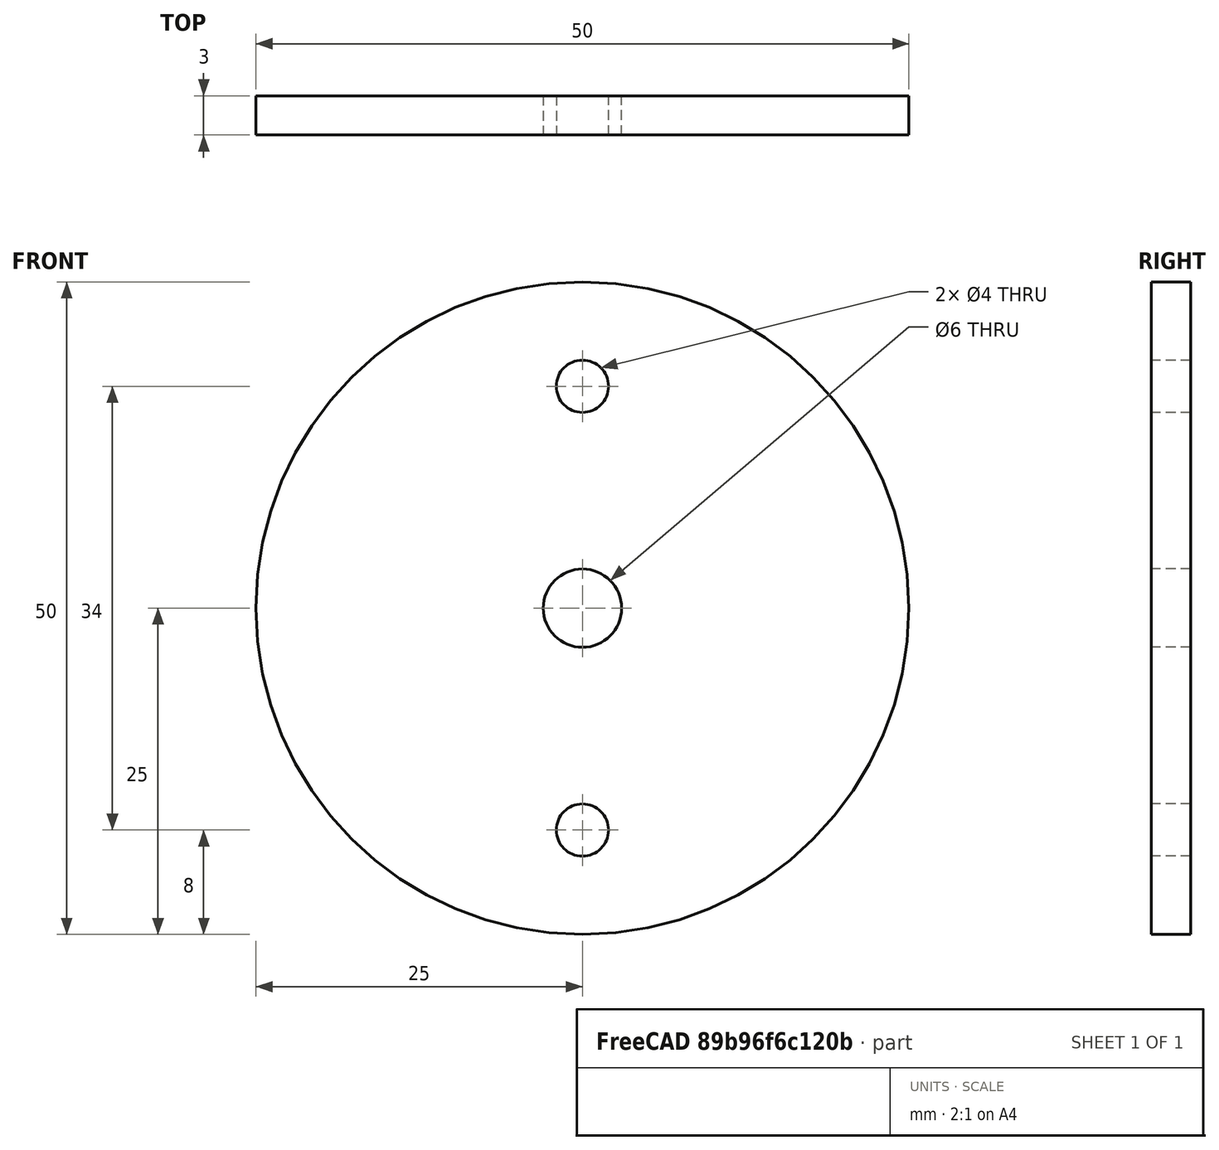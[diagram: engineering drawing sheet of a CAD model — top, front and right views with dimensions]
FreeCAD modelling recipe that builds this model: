
FCSTD DOCUMENT  (FreeCAD 0.15R4669 (Git))
Label: BR_plaqueRoue
License: All rights reserved
LicenseURL: http://en.wikipedia.org/wiki/All_rights_reserved
objects: Sketcher::SketchObject×1, Part::Extrusion×1
note: 2 computed .brp shape members not serialized (recipe doc carries the construction recipe); baked Part::Feature solids carry a one-line shape summary decoded from their .brp

FEATURE [Sketcher::SketchObject] Sketch  label="sektchPlaqueRoue"
  Placement = pos=(0,0,0) rot=(1,0,0;1.5708rad)
  sketch-geometry (4):
    g0: Circle CenterX=0 CenterY=0 CenterZ=0 NormalX=0 NormalY=0 NormalZ=1 Radius=25
    g1: Circle CenterX=0 CenterY=0 CenterZ=0 NormalX=0 NormalY=0 NormalZ=1 Radius=3
    g2: Circle CenterX=0 CenterY=17 CenterZ=0 NormalX=0 NormalY=0 NormalZ=1 Radius=2
    g3: Circle CenterX=0 CenterY=-17 CenterZ=0 NormalX=0 NormalY=0 NormalZ=1 Radius=2
  constraints (10):
    c: Coincident(g0,g-1)
    c: Radius(g0) = 25
    c: Coincident(g1,g-1)
    c: Radius(g1) = 3
    c: PointOnObject(g2,g-2)
    c: PointOnObject(g3,g-2)
    c: Symmetric(g3,g2,g-1)
    c: DistanceY(g-1,g2) = 17
    c: Radius(g2) = 2
    c: Equal(g3,g2)
FEATURE [Part::Extrusion] Extrude  label="plaqueRoue"
  Base = -> Sketch
  Dir = (0,3,0)
  Placement = pos=(0,-11,0) rot=(0,0,1;0rad)
  Solid = true
